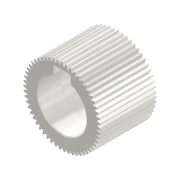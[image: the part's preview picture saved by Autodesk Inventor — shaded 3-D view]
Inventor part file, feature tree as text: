
AUTODESK INVENTOR PART (.ipt)
format: ipt  version: 2020.3 (Build 243373010, 373A)  size: 561,152 bytes
history: native  units: mm (DEFAULTED — no unit token found)
features: sketch x5, extrude x4, plane x3, other x3, fillet x1, chamfer x1
ambient origin geometry x8: Origin, YZ Plane, XZ Plane, XY Plane, X Axis, Y Axis, Z Axis, Center Point
bodies: Solid1 (feature_tree)
feature tree (17):
  extrude  "Extrusion1"  Depth=17.5mm TaperAngle=0.0deg
  plane  "Work Plane2"
  plane  "Work Plane8"
  plane  "Work Plane9"
  other  "Spur Gear"
  extrude  "Extrusion2"  Depth=10.0mm TaperAngle=0.0deg
  extrude  "Extrusion3"  Depth=0.571199mm TaperAngle=0.0deg
  extrude  "Extrusion4"  TaperAngle=0.0deg  [1 undecoded]
  fillet  "Fillet1"  Radius=14.7mm
  chamfer  "Chamfer1"  [1 undecoded]
  sketch  "Sketch1"  dims[d0=23.94mm d1=17.5mm d2=0.0mm]
  sketch  "Sketch2"  dims[d3=23.1mm d4=10.0mm d5=0.0mm]
  other  "Srf1"
  sketch  "Sketch3"  dims[d16=14.7mm d17=0.0mm d34=0.571199mm]
  sketch  "Sketch4"  dims[d39=0.0mm d41=0.0mm d43=14.7mm]
  sketch  "Sketch5"  dims[d46=14.7mm d47=0.0mm d48=0.0mm d49=15.0mm d50=0.0mm d51=0.0mm d52=17.0mm d53=10.0mm d54=0.0mm d55=5.0mm d61=5.0mm d62=20.0mm d63=0.0mm d64=0.25mm d65=0.25mm d66=2.0mm d67=45.0deg d68=17.1mm]
  other  "Pitch Diameter"
note: 2 required parameter values undecoded (feature->parameter linkage not recoverable at this tier; creation-order binding heuristic only, values carry confidence <= 0.55)
